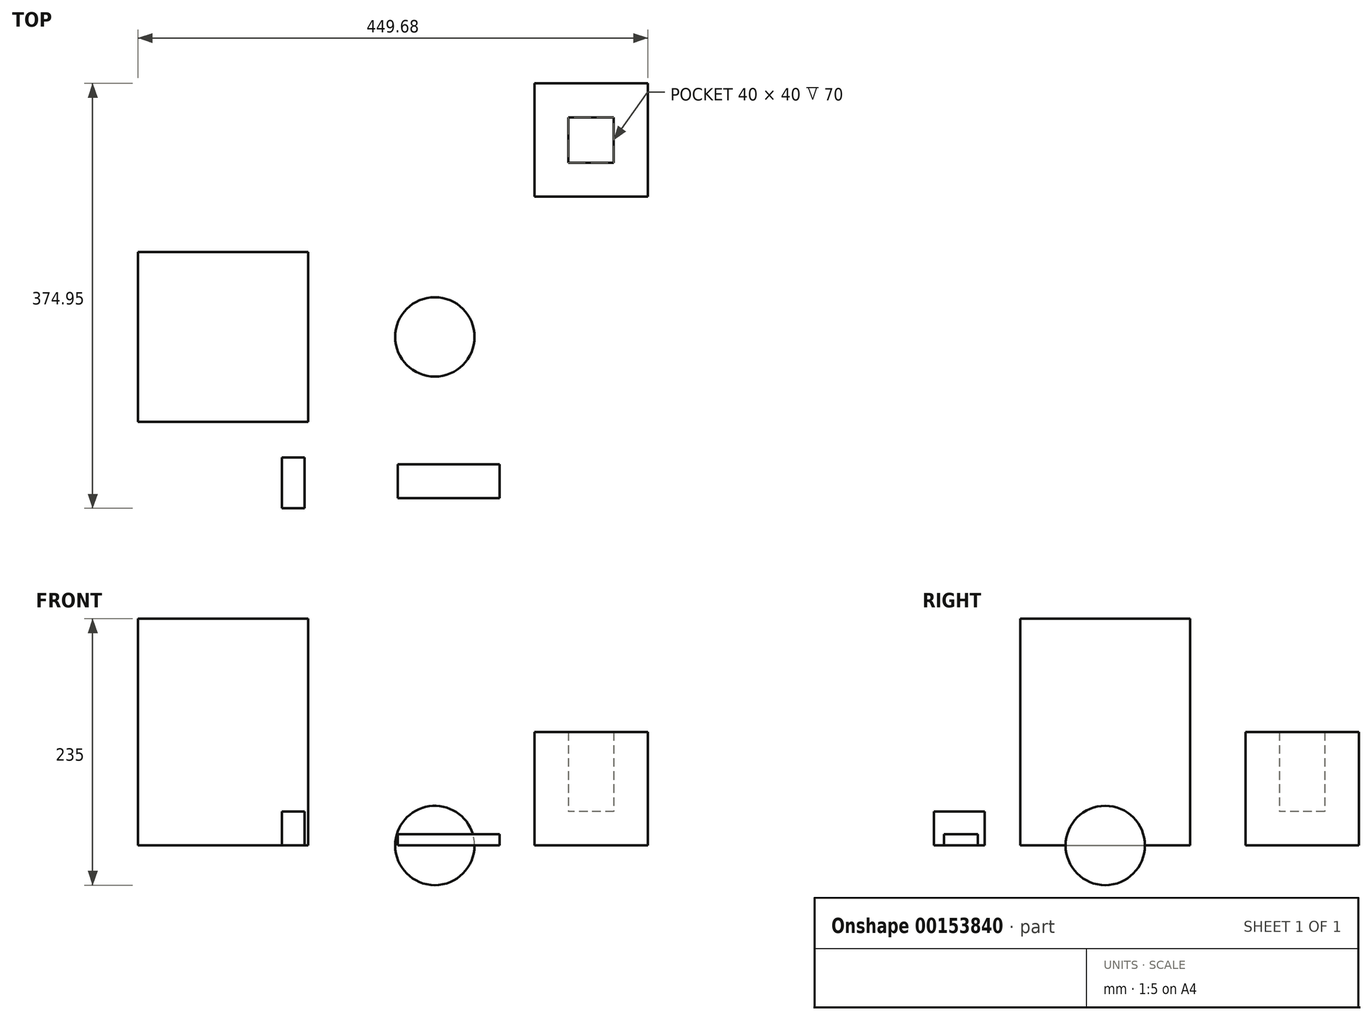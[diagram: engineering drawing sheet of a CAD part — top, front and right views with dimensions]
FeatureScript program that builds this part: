
annotation { "Feature Type Name" : "Feature", "Feature Type Description" : "" }
export const myFeature = defineFeature(function(context is Context, id is Id, definition is map)
    precondition{}
    {
        {
            var Q0;
            Q0=qCreatedBy(makeId("Top.planeOp"),FACE);
            var sketch = newSketch(context, id + "F0", { "sketchPlane" : qUnion([Q0])});
            skLineSegment(sketch, "E0.bottom", {"start": v(-75, -75) * mm, "end": v(75, -75) * mm});
            skLineSegment(sketch, "E0.top", {"start": v(-75, 75) * mm, "end": v(75, 75) * mm});
            skLineSegment(sketch, "E0.left", {"start": v(-75, -75) * mm, "end": v(-75, 75) * mm});
            skLineSegment(sketch, "E0.right", {"start": v(75, -75) * mm, "end": v(75, 75) * mm});
            skPoint(sketch, "E0.middle", {"position": v(0, 0) * mm});
            skSolve(sketch);
        }
        {
            var Q0;
            Q0 = qSketchRegion(id + "F0", true);
            extrude(context, id + "F1", {"entities" : qUnion([Q0]), "depth" : 200 * mm});
        }
        {
            var Q0;
            Q0=qCreatedBy(makeId("Top.planeOp"),FACE);
            var sketch = newSketch(context, id + "F2", { "sketchPlane" : qUnion([Q0])});
            skLineSegment(sketch, "E1", {"start": v(151.84, 0) * mm, "end": v(221.84, 0) * mm});
            skArc(sketch, "E2", {"start": v(221.84, 0) * mm, "mid": v(186.84, 35) * mm, "end": v(151.84, 0) * mm});
            skSolve(sketch);
        }
        {
            var Q0;
            Q0 = qSketchRegion(id + "F2", true);
            var Q1;
            Q1=sQuery(id+"F2.wireOp",EDGE,"E1");
            revolve(context, id + "F3", {"entities" : qUnion([Q0]), "axis" : qUnion([Q1]), "revolveType" : RevolveType.FULL});
        }
        {
            var Q0;
            Q0=qCreatedBy(makeId("Top.planeOp"),FACE);
            var sketch = newSketch(context, id + "F4", { "sketchPlane" : qUnion([Q0])});
            skLineSegment(sketch, "E3.bottom", {"start": v(51.83, -106.28) * mm, "end": v(71.83, -106.28) * mm});
            skLineSegment(sketch, "E3.top", {"start": v(51.83, -151.28) * mm, "end": v(71.83, -151.28) * mm});
            skLineSegment(sketch, "E3.left", {"start": v(51.83, -106.28) * mm, "end": v(51.83, -151.28) * mm});
            skLineSegment(sketch, "E3.right", {"start": v(71.83, -106.28) * mm, "end": v(71.83, -151.28) * mm});
            skSolve(sketch);
        }
        {
            var Q0;
            Q0=makeQuery(id+"F4.imprint","IMPRINT",FACE,{"disambiguationData":[TD([[makeQuery(id+"F4.imprint","IMPRINT",EDGE,{"derivedFrom":sQuery(id+"F4.wireOp",EDGE,"E3.bottom")}),-1.0]])]});
            extrude(context, id + "F5", {"entities" : qUnion([Q0]), "depth" : 30 * mm});
        }
        {
            var Q0;
            Q0=qCreatedBy(makeId("Top.planeOp"),FACE);
            var sketch = newSketch(context, id + "F6", { "sketchPlane" : qUnion([Q0])});
            skLineSegment(sketch, "E4.bottom", {"start": v(154.04, -112.28) * mm, "end": v(244.04, -112.28) * mm});
            skLineSegment(sketch, "E4.top", {"start": v(154.04, -142.28) * mm, "end": v(244.04, -142.28) * mm});
            skLineSegment(sketch, "E4.left", {"start": v(154.04, -112.28) * mm, "end": v(154.04, -142.28) * mm});
            skLineSegment(sketch, "E4.right", {"start": v(244.04, -112.28) * mm, "end": v(244.04, -142.28) * mm});
            skSolve(sketch);
        }
        {
            var Q0;
            Q0=makeQuery(id+"F6.imprint","IMPRINT",FACE,{"disambiguationData":[TD([[makeQuery(id+"F6.imprint","IMPRINT",EDGE,{"derivedFrom":sQuery(id+"F6.wireOp",EDGE,"E4.bottom")}),-1.0]])]});
            extrude(context, id + "F7", {"entities" : qUnion([Q0]), "depth" : 10 * mm});
        }
        {
            var Q0;
            Q0=qCreatedBy(makeId("Top.planeOp"),FACE);
            var sketch = newSketch(context, id + "F8", { "sketchPlane" : qUnion([Q0])});
            skLineSegment(sketch, "E5.bottom", {"start": v(374.68, 223.67) * mm, "end": v(274.68, 223.67) * mm});
            skLineSegment(sketch, "E5.top", {"start": v(374.68, 123.67) * mm, "end": v(274.68, 123.67) * mm});
            skLineSegment(sketch, "E5.left", {"start": v(374.68, 223.67) * mm, "end": v(374.68, 123.67) * mm});
            skLineSegment(sketch, "E5.right", {"start": v(274.68, 223.67) * mm, "end": v(274.68, 123.67) * mm});
            skSolve(sketch);
        }
        {
            var Q0;
            Q0=makeQuery(id+"F8.imprint","IMPRINT",FACE,{"disambiguationData":[TD([[makeQuery(id+"F8.imprint","IMPRINT",EDGE,{"derivedFrom":sQuery(id+"F8.wireOp",EDGE,"E5.bottom")}),1.0]])]});
            extrude(context, id + "F9", {"entities" : qUnion([Q0]), "depth" : 100 * mm});
        }
        {
            var Q0;
            Q0=makeQuery(id+"F9.opExtrude","CAP_FACE",FACE,{"disambiguationData":[OSD([sQuery(id+"F8.wireOp",EDGE,"E5.bottom"),sQuery(id+"F8.wireOp",EDGE,"E5.top"),sQuery(id+"F8.wireOp",EDGE,"E5.left"),sQuery(id+"F8.wireOp",EDGE,"E5.right")])],"isStart":false});
            shell(context, id + "F10", {"entities" : qUnion([Q0]), "thickness" : 30 * mm});
        }
    });
